# Revit family: CADS_AIRFLOWdev_AirTerminal_RoofSlate_Exhaust
name_source: partatom
category: Air Terminals
revit_build: Autodesk Revit 2015 (Build: 20160512_0715(x64)
units: mm (PartAtom-declared; Revit-internal decimal feet)

## types (2) — shared parameters
6MonthlyMaintenance = Visually inspect system, clean the fan and ducting if necessary
AirflowRateRange = 0-61
AssetType = Fixed
CEApproval = Yes
Color = Silver
Constituents = Silver
Default Elevation = 1219 mm
DurationUnit = Years
Exclusions = Incorrect Use / Incorrect Installation / Installed by a non-accredited electrician. Customer abuse.
FaceType = LOUVERED
FlowControlType = NONE
Grade = Virgin
HasIntegralControl = No
HasSoundAttenuator = No
HasThermalInsulation = No
ISO140001 = Yes
ISO90001 = Yes
IsExtendedWarranty = No
Manufacturer = Airflow Developments Ltd
ManufacturerAddress = Aidelle House
Lancaster Road
Cressex Business Park
High Wycombe
Bucks
HP123QP
ManufacturerTelephone = 01494 525252
ManufacturerWebsite = www.airflow.com
Material = Aluminium
MountingType = SURFACE
NBSCode = 90-75-50/370 Air terminals;
NominalHeight = 2 mm  [stored 0.00656168 ft]
PointOfContact = Airflow Developments Ltd
ProductionYear = 2017
ReplacementCost = 77.46
RoofSlate_Connector = CADS_AirFlow_Black
RoofSlate_Cover = CADS_Airflow_Chrome
ServiceLifeDuration = 10
ServiceLifeType = EXPECTEDSERVICELIFE
Shape = Rectangular
Uniclass2015 = Pr_65_70_46_01
WarrantyContent = Replacement of part if faulty
WarrantyGuarantor = Airflow Developments Ltd
WarrantyPeriod = 2
zero-valued in all types: NumberOfSlots

## per-type parameters (varying)
| type | A | Description | GlobalTradeItemNumber | GrossWeight | ModelLabel | ModelReference | NominalLength | NominalWidth | ShippingWeight | Size |
| 450 | 450 mm  [stored 1.47638 ft] | 450mm square aluminium roof slate (pitched roof) | 5019009310459 | 0.03 kg | 450mm square aluminium roof slate (pitched roof) | 9004597 | 450 mm  [stored 1.47638 ft] | 450 mm  [stored 1.47638 ft] | 0.04 kg | 450 x 450 x 2 |
| 600 | 600 mm  [stored 1.9685 ft] | 600mm square aluminium roof slate (pitched roof) |  | 0.05 kg | 600mm square aluminium roof slate (pitched roof) | 9004598 | 600 mm  [stored 1.9685 ft] | 600 mm  [stored 1.9685 ft] | 0.06 kg | 600 x 600 x 2 |

note: [stored X ft] marks values corroborated as IEEE doubles in the binary element streams (Revit-internal decimal feet)

## geometry (parser evidence)
native form markers: Blend x16, Sweep x2
no freeform markers — native parametric forms only
